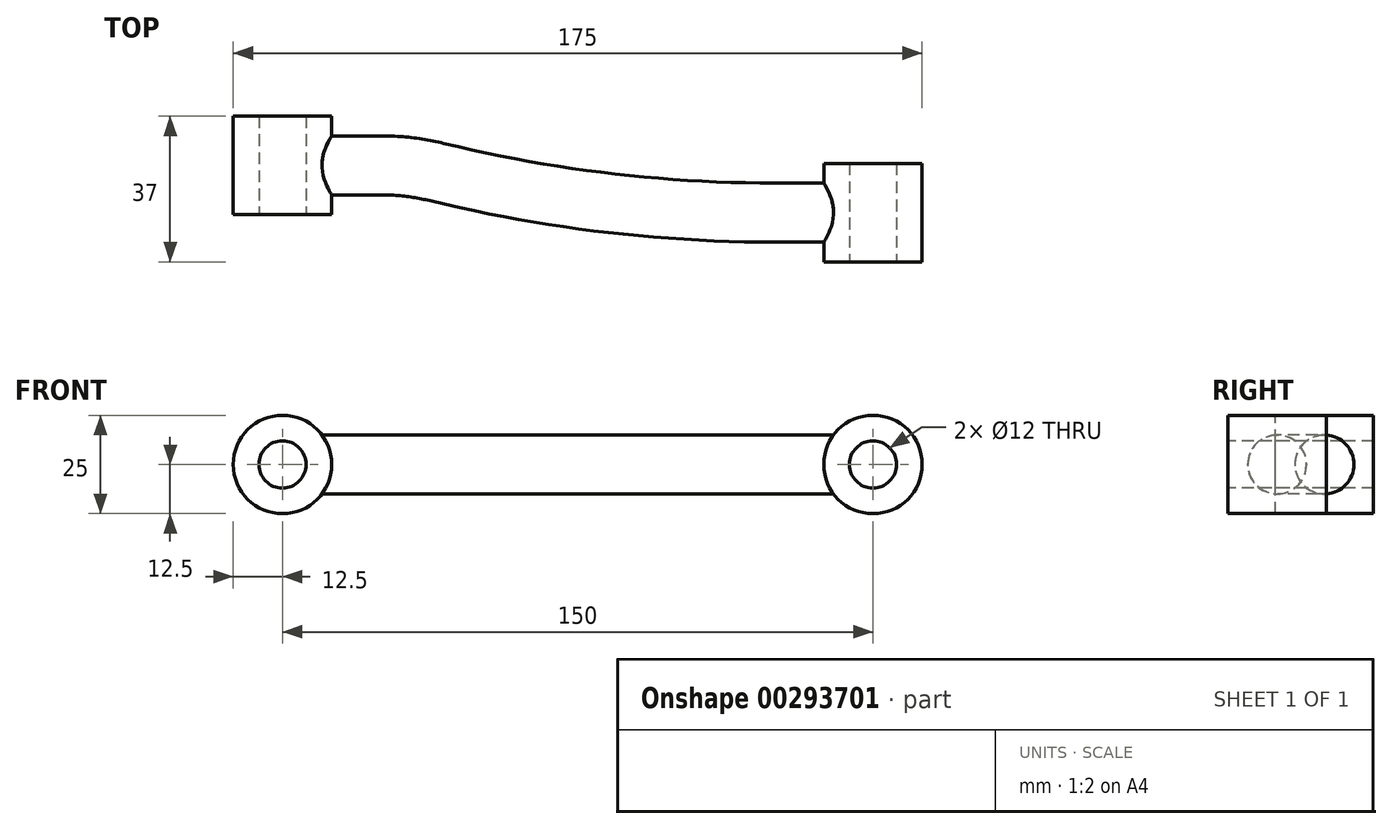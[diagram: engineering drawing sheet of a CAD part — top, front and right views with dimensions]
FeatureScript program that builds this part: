
annotation { "Feature Type Name" : "Feature", "Feature Type Description" : "" }
export const myFeature = defineFeature(function(context is Context, id is Id, definition is map)
    precondition{}
    {
        {
            var Q0;
            Q0=qCreatedBy(makeId("Top.planeOp"),FACE);
            var sketch = newSketch(context, id + "F0", { "sketchPlane" : qUnion([Q0])});
            skLineSegment(sketch, "E0", {"start": v(0, 0) * mm, "end": v(150, 0) * mm, "construction": true});
            skLineSegment(sketch, "E1", {"start": v(150, 0) * mm, "end": v(150, -12) * mm, "construction": true});
            skLineSegment(sketch, "E2", {"start": v(150, -12) * mm, "end": v(125, -12) * mm});
            skLineSegment(sketch, "E3", {"start": v(0, 0) * mm, "end": v(25, 0) * mm});
            skArc(sketch, "E4", {"start": v(25, 0) * mm, "mid": v(32.15, -0.43) * mm, "end": v(39.2, -1.7) * mm});
            skArc(sketch, "E5", {"start": v(39.2, -1.7) * mm, "mid": v(81.79, -9.42) * mm, "end": v(125, -12) * mm});
            skSolve(sketch);
        }
        {
            var Q0;
            Q0=qCreatedBy(makeId("Right.planeOp"),FACE);
            var sketch = newSketch(context, id + "F1", { "sketchPlane" : qUnion([Q0])});
            skCircle(sketch, "E6", {"center": v(0, 0) * mm, "radius": 7.5 * mm});
            skSolve(sketch);
        }
        {
            var Q0;
            Q0=makeQuery(id+"F1.imprint","IMPRINT",FACE,{"disambiguationData":[TD([[makeQuery(id+"F1.imprint","IMPRINT",EDGE,{"derivedFrom":sQuery(id+"F1.wireOp",EDGE,"E6")}),1.0]])]});
            var Q1;
            Q1 = qConstructionFilter(qBodyType(qCreatedBy(id + "F0" ,EDGE), BodyType.WIRE), ConstructionObject.NO);
            sweep(context, id + "F2", {"profiles" : qUnion([Q0]), "path" : qUnion([Q1])});
        }
        {
            var Q0;
            Q0=qCreatedBy(makeId("Front.planeOp"),FACE);
            var sketch = newSketch(context, id + "F3", { "sketchPlane" : qUnion([Q0])});
            skCircle(sketch, "E7", {"center": v(0, 0) * mm, "radius": 12.5 * mm});
            skSolve(sketch);
        }
        {
            var Q0;
            Q0 = qSketchRegion(id + "F3", true);
            extrude(context, id + "F4", {"entities" : qUnion([Q0]), "operationType" : NewBodyOperationType.ADD, "endBound" : BoundingType.SYMMETRIC, "depth" : 25 * mm});
        }
        {
            var Q0;
            Q0=makeQuery(id+"F4.opExtrude","CAP_FACE",FACE,{"disambiguationData":[OSD([sQuery(id+"F3.wireOp",EDGE,"E7")])],"isStart":false});
            var sketch = newSketch(context, id + "F5", { "sketchPlane" : qUnion([Q0])});
            skCircle(sketch, "E8", {"center": v(0, 0) * mm, "radius": 6 * mm});
            skSolve(sketch);
        }
        {
            var Q0;
            Q0 = qSketchRegion(id + "F5", true);
            extrude(context, id + "F6", {"entities" : qUnion([Q0]), "operationType" : NewBodyOperationType.REMOVE, "oppositeDirection" : true, "depth" : 25 * mm});
        }
        {
            var Q0;
            Q0=qCreatedBy(makeId("Front.planeOp"),FACE);
            cPlane(context, id + "F7", {"entities" : qUnion([Q0]), "cplaneType" : CPlaneType.OFFSET, "offset" : 12 * mm, "width" : 150 * mm, "height" : 150 * mm});
        }
        {
            var Q0;
            Q0=qCreatedBy(id+"F7.planeOp",FACE);
            var sketch = newSketch(context, id + "F8", { "sketchPlane" : qUnion([Q0])});
            skLineSegment(sketch, "E9", {"start": v(150, -7.5) * mm, "end": v(125, -7.5) * mm});
            skLineSegment(sketch, "E10", {"start": v(125, 7.5) * mm, "end": v(150, 7.5) * mm});
            skLineSegment(sketch, "E11", {"start": v(150, 7.5) * mm, "end": v(150, -7.5) * mm});
            skCircle(sketch, "E12", {"center": v(150, 0) * mm, "radius": 12.5 * mm});
            skSolve(sketch);
        }
        {
            var Q0;
            {var subQ0=sQuery(id+"F8.wireOp",EDGE,"E11");Q0=makeQuery(id+"F8.imprint","IMPRINT",FACE,{"disambiguationData":[TD([[makeQuery(id+"F8.imprint","IMPRINT",EDGE,{"derivedFrom":subQ0}),-1.0]])]});}
            var Q1;
            {var subQ0=sQuery(id+"F8.wireOp",EDGE,"E11");Q1=makeQuery(id+"F8.imprint","IMPRINT",FACE,{"disambiguationData":[TD([[makeQuery(id+"F8.imprint","IMPRINT",EDGE,{"derivedFrom":subQ0}),1.0]])]});}
            extrude(context, id + "F9", {"entities" : qUnion([Q0, Q1]), "operationType" : NewBodyOperationType.ADD, "endBound" : BoundingType.SYMMETRIC, "oppositeDirection" : true, "depth" : 25 * mm});
        }
        {
            var Q0;
            Q0=makeQuery(id+"F9.opExtrude","CAP_FACE",FACE,{"disambiguationData":[OSD([sQuery(id+"F8.wireOp",EDGE,"E12")])],"isStart":true});
            var sketch = newSketch(context, id + "F10", { "sketchPlane" : qUnion([Q0])});
            skCircle(sketch, "E13", {"center": v(150, 0) * mm, "radius": 6 * mm});
            skSolve(sketch);
        }
        {
            var Q0;
            Q0 = qSketchRegion(id + "F10", true);
            extrude(context, id + "F11", {"entities" : qUnion([Q0]), "operationType" : NewBodyOperationType.REMOVE, "oppositeDirection" : true, "depth" : 25 * mm});
        }
    });
